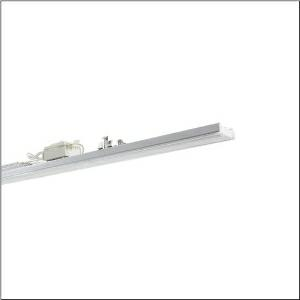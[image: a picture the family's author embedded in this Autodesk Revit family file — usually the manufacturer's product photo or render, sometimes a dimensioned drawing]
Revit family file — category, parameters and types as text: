
# Revit family: licross_r__21_recessed_mo_52te1ecn485g_1eda
name_source: partatom
category: Lighting Fixtures
units: mm (PartAtom-declared; Revit-internal decimal feet)

## family parameters
Cut with Voids When Loaded = No
Host = Face
Light Source = No
Part Type = Normal
Room Calculation Point = No
Round Connector Dimension = Use Diameter
Shared = No

## types (1)
- --- (1 x LED, 8960 lm, 49.9 W, 4000K)
    Apparent Load = 50 VA
    CIE Flux Codes = 85 95 99 100 100
    Color Rendering = 80
    Color Temperature = 4000K
    Default Elevation = 1800 mm
    Description = Licross® 21 Recessed MO, luminaire insert, of sheet steel, galvanised, coil coated, white, length: 1.500mm, width: 66mm, height: 67mm, LED rated luminous flux: 8.960lm, light colour: 840, control gear: ON/OFF Multilumen, CLOi, control gear: ECG Multilumen, with plug, 3-pole, with phase selection, mains connection: 220..240V, AC, 50/60Hz, start of lifetime: 50W, end of service life: 61W, internal wiring halogen-free, primary light control with lens, of plastic, primary optical cover: cover, of PMMA, light emission: direct distribution, primary light characteristic: symmetric, protection rating (complete): IP54, insulation class (complete): insulation class I (protective earthing), certification: CE, ENEC, VDE, UKCA, protection symbol: D if used in an environment with non-conductive dust loads with corresponding accessories, impact resistance: IK06, permissible ambient temperature for indoor applications: -35..+40°C, corresponds to IFS (International Featured Standards) requirements for safety and quality in the food industry, reducing of maximum allowable ambient temperature of 5°C with ceiling mounting, LABS conformity tested according to VDMA 24364:2018-05, packaging unit: 1 piece
    Height = 58 mm
    Lamp = 1 x LED
    Lamp Light Flux = 8960 lm
    Lamp Power = 49.9 W
    Lamp count = 1
    Length = 1500 mm
    Luminous efficacy = 180 lm/W
    Manufacturer = Siteco
    ModVariant = No
    Model = 52TE1ECN485G
    Mounting Place = Ceiling
    Mounting Type = Pendant
    Number of Poles = 1
    OnlyDefault = Yes
    Power Factor = 1
    Product Name = Licross® 21 Recessed MO
    Product group = luminaire insert | ceiling pendant
    ProductGroupID = 902
    Protection Class = Protection class I
    Protection Degree = IP 54
    RLX_Detail_Level = 1
    RLX_Emergency_Light_Flux = 0 lm
    RLX_Emergency_Type = 0
    RLX_Emergency_Type_DB = No
    RlxData = <blob elided: 22445 chars, md5=64879d55>
    Socket = socket
    Standby Power = 0 W
    System Light Flux = 8960 lm
    System Power = 50 W
    Type Comments = factory setting: luminous flux: 100 % | (A | C | E) | 116 mA
    Type Image = l_1296930.jpg
    URL = http://relux.com
    VarID = @adj_131323
    Voltage = 0 V
    Weight = 0.00 kg
    Width = 66 mm

## geometry (parser evidence)
native form markers: Blend x4, Sweep x14
no freeform markers — native parametric forms only
